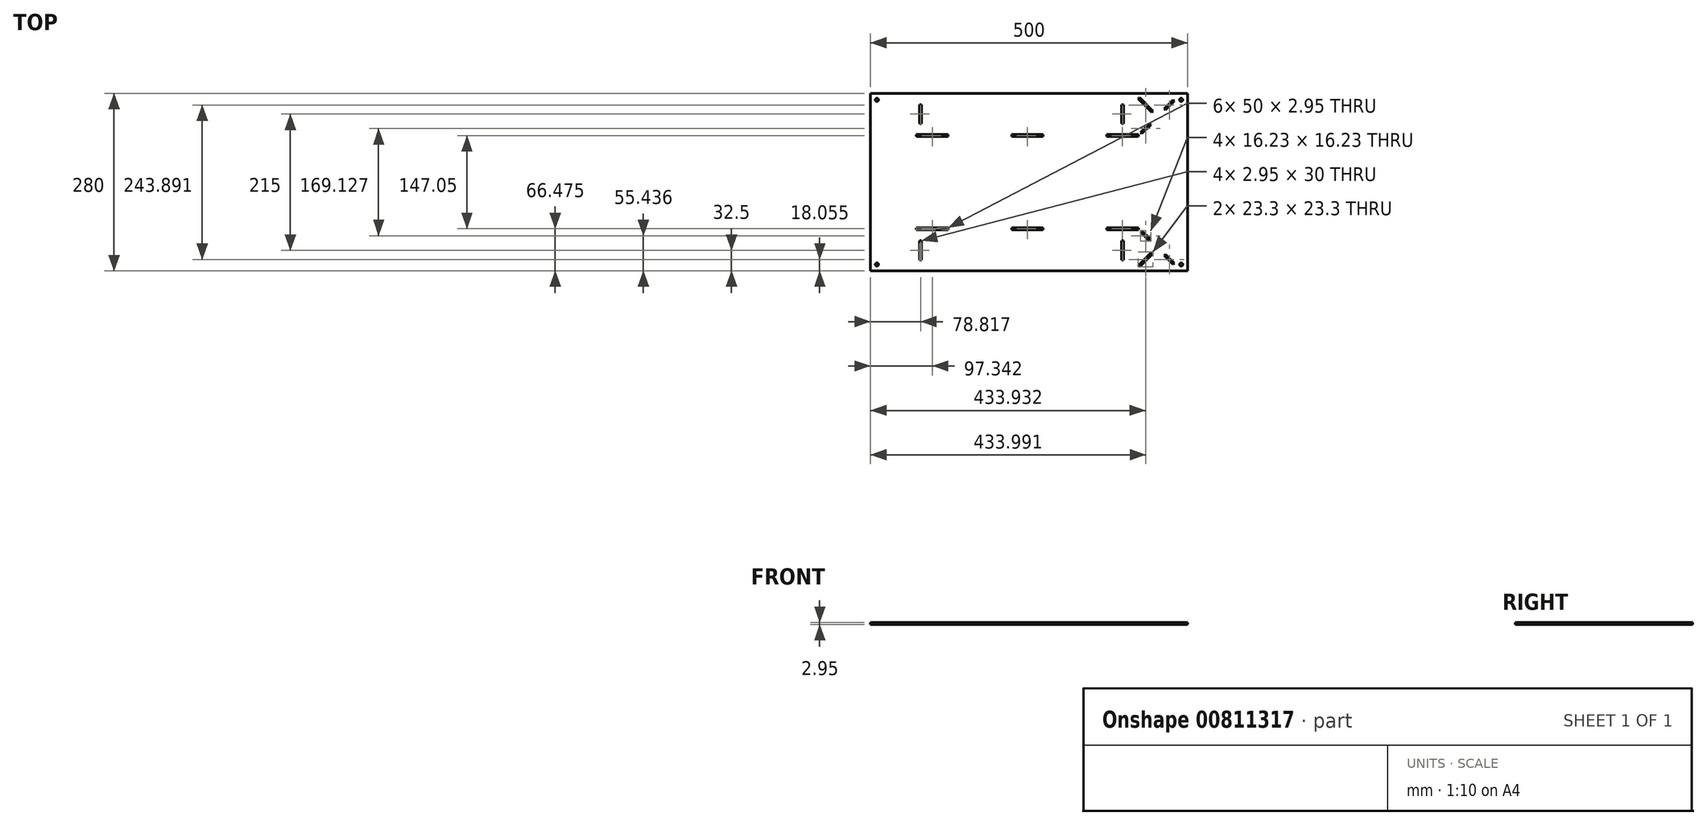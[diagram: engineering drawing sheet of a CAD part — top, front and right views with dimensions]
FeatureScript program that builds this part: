
annotation { "Feature Type Name" : "Feature", "Feature Type Description" : "" }
export const myFeature = defineFeature(function(context is Context, id is Id, definition is map)
    precondition{}
    {
        {
            var Q0;
            Q0=qCreatedBy(makeId("Top.planeOp"),FACE);
            var sketch = newSketch(context, id + "F0", { "sketchPlane" : qUnion([Q0])});
            skLineSegment(sketch, "E0.bottom", {"start": v(12.1, 0) * mm, "end": v(462.1, 0) * mm});
            skLineSegment(sketch, "E0.top", {"start": v(62.1, 280) * mm, "end": v(462.1, 280) * mm});
            skLineSegment(sketch, "E0.right", {"start": v(462.1, 0) * mm, "end": v(462.1, 280) * mm});
            skLineSegment(sketch, "E1.bottom", {"start": v(184.43, 215) * mm, "end": v(234.43, 215) * mm});
            skLineSegment(sketch, "E1.top", {"start": v(184.43, 212.05) * mm, "end": v(234.43, 212.05) * mm});
            skLineSegment(sketch, "E1.left", {"start": v(184.43, 215) * mm, "end": v(184.43, 212.05) * mm});
            skLineSegment(sketch, "E1.right", {"start": v(234.43, 215) * mm, "end": v(234.43, 212.05) * mm});
            skLineSegment(sketch, "E2.MirrorCS", {"start": v(334.43, 215) * mm, "end": v(334.43, 215) * mm});
            skLineSegment(sketch, "E3.MirrorCS", {"start": v(134.43, 65) * mm, "end": v(234.43, 65) * mm});
            skLineSegment(sketch, "E4.MirrorCS", {"start": v(334.43, 65) * mm, "end": v(334.43, 65) * mm});
            skLineSegment(sketch, "E5.bottom", {"start": v(358.36, 262.5) * mm, "end": v(361.3, 262.5) * mm});
            skLineSegment(sketch, "E5.top", {"start": v(358.36, 232.5) * mm, "end": v(361.3, 232.5) * mm});
            skLineSegment(sketch, "E5.left", {"start": v(358.36, 262.5) * mm, "end": v(358.36, 232.5) * mm});
            skLineSegment(sketch, "E5.right", {"start": v(361.3, 262.5) * mm, "end": v(361.3, 232.5) * mm});
            skLineSegment(sketch, "E6.bottom", {"start": v(334.43, 215) * mm, "end": v(384.43, 215) * mm});
            skLineSegment(sketch, "E6.top", {"start": v(334.43, 212.05) * mm, "end": v(384.43, 212.05) * mm});
            skLineSegment(sketch, "E6.left", {"start": v(334.43, 215) * mm, "end": v(334.43, 212.05) * mm});
            skLineSegment(sketch, "E6.right", {"start": v(384.43, 215) * mm, "end": v(384.43, 212.05) * mm});
            skLineSegment(sketch, "E7.bottom", {"start": v(234.43, 65) * mm, "end": v(184.43, 65) * mm});
            skLineSegment(sketch, "E7.top", {"start": v(234.43, 67.95) * mm, "end": v(184.43, 67.95) * mm});
            skLineSegment(sketch, "E7.left", {"start": v(234.43, 65) * mm, "end": v(234.43, 67.95) * mm});
            skLineSegment(sketch, "E7.right", {"start": v(184.43, 65) * mm, "end": v(184.43, 67.95) * mm});
            skLineSegment(sketch, "E8.bottom", {"start": v(334.43, 65) * mm, "end": v(384.43, 65) * mm});
            skLineSegment(sketch, "E8.top", {"start": v(334.43, 67.95) * mm, "end": v(384.43, 67.95) * mm});
            skLineSegment(sketch, "E8.left", {"start": v(334.43, 65) * mm, "end": v(334.43, 67.95) * mm});
            skLineSegment(sketch, "E8.right", {"start": v(384.43, 65) * mm, "end": v(384.43, 67.95) * mm});
            skLineSegment(sketch, "E9.bottom", {"start": v(358.36, 47.5) * mm, "end": v(361.3, 47.5) * mm});
            skLineSegment(sketch, "E9.top", {"start": v(358.36, 17.5) * mm, "end": v(361.3, 17.5) * mm});
            skLineSegment(sketch, "E9.left", {"start": v(358.36, 47.5) * mm, "end": v(358.36, 17.5) * mm});
            skLineSegment(sketch, "E9.right", {"start": v(361.3, 47.5) * mm, "end": v(361.3, 17.5) * mm});
            skLineSegment(sketch, "E10.bottom", {"start": v(62.1, 280) * mm, "end": v(-37.9, 280) * mm});
            skLineSegment(sketch, "E10.top", {"start": v(12.1, 0) * mm, "end": v(-37.9, 0) * mm});
            skLineSegment(sketch, "E10.right", {"start": v(-37.9, 280) * mm, "end": v(-37.9, 0) * mm});
            skLineSegment(sketch, "E11.bottom", {"start": v(84.43, 215) * mm, "end": v(34.43, 215) * mm});
            skLineSegment(sketch, "E11.top", {"start": v(84.43, 212.05) * mm, "end": v(34.43, 212.05) * mm});
            skLineSegment(sketch, "E11.left", {"start": v(84.43, 215) * mm, "end": v(84.43, 212.05) * mm});
            skLineSegment(sketch, "E11.right", {"start": v(34.43, 215) * mm, "end": v(34.43, 212.05) * mm});
            skLineSegment(sketch, "E12.bottom", {"start": v(84.43, 67.95) * mm, "end": v(34.43, 67.95) * mm});
            skLineSegment(sketch, "E12.top", {"start": v(84.43, 65) * mm, "end": v(34.43, 65) * mm});
            skLineSegment(sketch, "E12.left", {"start": v(84.43, 67.95) * mm, "end": v(84.43, 65) * mm});
            skLineSegment(sketch, "E12.right", {"start": v(34.43, 67.95) * mm, "end": v(34.43, 65) * mm});
            skLineSegment(sketch, "E13.bottom", {"start": v(39.43, 262.5) * mm, "end": v(42.38, 262.5) * mm});
            skLineSegment(sketch, "E13.top", {"start": v(39.43, 232.5) * mm, "end": v(42.38, 232.5) * mm});
            skLineSegment(sketch, "E13.left", {"start": v(39.43, 262.5) * mm, "end": v(39.43, 232.5) * mm});
            skLineSegment(sketch, "E13.right", {"start": v(42.38, 262.5) * mm, "end": v(42.38, 232.5) * mm});
            skLineSegment(sketch, "E14.bottom", {"start": v(39.43, 47.5) * mm, "end": v(42.38, 47.5) * mm});
            skLineSegment(sketch, "E14.top", {"start": v(39.43, 17.5) * mm, "end": v(42.38, 17.5) * mm});
            skLineSegment(sketch, "E14.left", {"start": v(39.43, 47.5) * mm, "end": v(39.43, 17.5) * mm});
            skLineSegment(sketch, "E14.right", {"start": v(42.38, 47.5) * mm, "end": v(42.38, 17.5) * mm});
            skSolve(sketch);
        }
        {
            var Q0;
            Q0=makeQuery(id+"F0.imprint","IMPRINT",FACE,{"disambiguationData":[TD([[makeQuery(id+"F0.imprint","IMPRINT",EDGE,{"derivedFrom":sQuery(id+"F0.wireOp",EDGE,"E0.bottom")}),1.0]])]});
            extrude(context, id + "F1", {"entities" : qUnion([Q0]), "depth" : 2.95 * mm, "offsetDistance" : 25 * mm});
        }
        {
            var Q0;
            Q0=makeQuery(id+"F1.opExtrude","CAP_FACE",FACE,{"disambiguationData":[OSD([sQuery(id+"F0.wireOp",EDGE,"E0.bottom"),sQuery(id+"F0.wireOp",EDGE,"E0.top"),sQuery(id+"F0.wireOp",EDGE,"E0.left"),sQuery(id+"F0.wireOp",EDGE,"E0.right"),sQuery(id+"F0.wireOp",EDGE,"E1.bottom"),sQuery(id+"F0.wireOp",EDGE,"E1.top"),sQuery(id+"F0.wireOp",EDGE,"E1.left"),sQuery(id+"F0.wireOp",EDGE,"E1.right"),sQuery(id+"F0.wireOp",EDGE,"e73540e0-437e-4d11-b89e-325f1f7d4c790.MirrorCS"),sQuery(id+"F0.wireOp",EDGE,"E2.MirrorCS"),sQuery(id+"F0.wireOp",EDGE,"06532218-7f8b-4a41-8e3c-2a9fed56a3b10.MirrorCS"),sQuery(id+"F0.wireOp",EDGE,"7cb798fc-15e8-495b-8a35-73028b4edfa90.MirrorCS"),sQuery(id+"F0.wireOp",EDGE,"545d7cc9-1fc7-4841-af53-376eaec099370.MirrorCS"),sQuery(id+"F0.wireOp",EDGE,"E3.MirrorCS"),sQuery(id+"F0.wireOp",EDGE,"9b8ca559-61c4-4ae6-86d6-e5e959e65d2c0.MirrorCS"),sQuery(id+"F0.wireOp",EDGE,"461afd8d-256b-4b3b-8858-7b4be28ac2ee0.MirrorCS"),sQuery(id+"F0.wireOp",EDGE,"ccdc6204-bf97-4cc3-8a27-938706aa7f700.MirrorCS"),sQuery(id+"F0.wireOp",EDGE,"E4.MirrorCS"),sQuery(id+"F0.wireOp",EDGE,"de380e3f-fddb-4eb0-9c14-f8c98a16e2c70.MirrorCS"),sQuery(id+"F0.wireOp",EDGE,"ee423979-f3e1-44e8-98c6-b9dc3032ede40.MirrorCS"),sQuery(id+"F0.wireOp",EDGE,"E5.bottom"),sQuery(id+"F0.wireOp",EDGE,"E5.top"),sQuery(id+"F0.wireOp",EDGE,"E5.left"),sQuery(id+"F0.wireOp",EDGE,"E5.right"),sQuery(id+"F0.wireOp",EDGE,"2a4d6bfd-6cea-46ef-a5a2-565ee4e24cbc0.MirrorCS"),sQuery(id+"F0.wireOp",EDGE,"e7e3dcee-2f9a-4279-8a5c-00eaed48cf630.MirrorCS"),sQuery(id+"F0.wireOp",EDGE,"b1a6a120-30f8-47bb-a578-e070e3f1ff540.MirrorCS"),sQuery(id+"F0.wireOp",EDGE,"80d5920c-4993-49ba-a786-e7242780b6720.MirrorCS")])],"isStart":false});
            var sketch = newSketch(context, id + "F2", { "sketchPlane" : qUnion([Q0])});
            skPoint(sketch, "E15", {"position": v(-27.9, 10) * mm});
            skPoint(sketch, "E16", {"position": v(-27.9, 270) * mm});
            skPoint(sketch, "E17", {"position": v(452.1, 270) * mm});
            skPoint(sketch, "E18", {"position": v(452.1, 10) * mm});
            skSolve(sketch);
        }
        {
            var Q0;
            Q0=sQuery(id+"F2.wireOp",VERTEX,"E15");
            var Q1;
            Q1=sQuery(id+"F2.wireOp",VERTEX,"E16");
            var Q2;
            Q2=sQuery(id+"F2.wireOp",VERTEX,"E18");
            var Q3;
            Q3=sQuery(id+"F2.wireOp",VERTEX,"E17");
            var Q4;
            Q4=makeQuery(id+"F1.opExtrude","SWEPT_BODY",BODY,{"disambiguationData":[OSD([sQuery(id+"F0.wireOp",EDGE,"E0.bottom"),sQuery(id+"F0.wireOp",EDGE,"E0.top"),sQuery(id+"F0.wireOp",EDGE,"E0.left"),sQuery(id+"F0.wireOp",EDGE,"E0.right"),sQuery(id+"F0.wireOp",EDGE,"E1.bottom"),sQuery(id+"F0.wireOp",EDGE,"E1.top"),sQuery(id+"F0.wireOp",EDGE,"E1.left"),sQuery(id+"F0.wireOp",EDGE,"E1.right"),sQuery(id+"F0.wireOp",EDGE,"e73540e0-437e-4d11-b89e-325f1f7d4c790.MirrorCS"),sQuery(id+"F0.wireOp",EDGE,"E2.MirrorCS"),sQuery(id+"F0.wireOp",EDGE,"06532218-7f8b-4a41-8e3c-2a9fed56a3b10.MirrorCS"),sQuery(id+"F0.wireOp",EDGE,"7cb798fc-15e8-495b-8a35-73028b4edfa90.MirrorCS"),sQuery(id+"F0.wireOp",EDGE,"545d7cc9-1fc7-4841-af53-376eaec099370.MirrorCS"),sQuery(id+"F0.wireOp",EDGE,"E3.MirrorCS"),sQuery(id+"F0.wireOp",EDGE,"9b8ca559-61c4-4ae6-86d6-e5e959e65d2c0.MirrorCS"),sQuery(id+"F0.wireOp",EDGE,"461afd8d-256b-4b3b-8858-7b4be28ac2ee0.MirrorCS"),sQuery(id+"F0.wireOp",EDGE,"ccdc6204-bf97-4cc3-8a27-938706aa7f700.MirrorCS"),sQuery(id+"F0.wireOp",EDGE,"E4.MirrorCS"),sQuery(id+"F0.wireOp",EDGE,"de380e3f-fddb-4eb0-9c14-f8c98a16e2c70.MirrorCS"),sQuery(id+"F0.wireOp",EDGE,"ee423979-f3e1-44e8-98c6-b9dc3032ede40.MirrorCS"),sQuery(id+"F0.wireOp",EDGE,"E5.bottom"),sQuery(id+"F0.wireOp",EDGE,"E5.top"),sQuery(id+"F0.wireOp",EDGE,"E5.left"),sQuery(id+"F0.wireOp",EDGE,"E5.right"),sQuery(id+"F0.wireOp",EDGE,"2a4d6bfd-6cea-46ef-a5a2-565ee4e24cbc0.MirrorCS"),sQuery(id+"F0.wireOp",EDGE,"e7e3dcee-2f9a-4279-8a5c-00eaed48cf630.MirrorCS"),sQuery(id+"F0.wireOp",EDGE,"b1a6a120-30f8-47bb-a578-e070e3f1ff540.MirrorCS"),sQuery(id+"F0.wireOp",EDGE,"80d5920c-4993-49ba-a786-e7242780b6720.MirrorCS")])]});
            hole(context, id + "F3", {"style" : HoleStyle.SIMPLE, "endStyle" : HoleEndStyle.THROUGH, "holeDiameter" : 5 * mm, "majorDiameter" : 5 * mm, "isTappedThrough" : true, "tappedDepth" : 12 * mm, "tapClearance" : 3, "locations" : qUnion([Q0, Q1, Q2, Q3]), "scope" : qUnion([Q4])});
        }
        {
            var Q0;
            Q0=makeQuery(id+"F1.opExtrude","CAP_FACE",FACE,{"disambiguationData":[OSD([sQuery(id+"F0.wireOp",EDGE,"E0.bottom"),sQuery(id+"F0.wireOp",EDGE,"E0.top"),sQuery(id+"F0.wireOp",EDGE,"E0.left"),sQuery(id+"F0.wireOp",EDGE,"E0.right"),sQuery(id+"F0.wireOp",EDGE,"E1.bottom"),sQuery(id+"F0.wireOp",EDGE,"E1.top"),sQuery(id+"F0.wireOp",EDGE,"E1.left"),sQuery(id+"F0.wireOp",EDGE,"E1.right"),sQuery(id+"F0.wireOp",EDGE,"E5.bottom"),sQuery(id+"F0.wireOp",EDGE,"E5.top"),sQuery(id+"F0.wireOp",EDGE,"E5.left"),sQuery(id+"F0.wireOp",EDGE,"E5.right"),sQuery(id+"F0.wireOp",EDGE,"E6.bottom"),sQuery(id+"F0.wireOp",EDGE,"E6.top"),sQuery(id+"F0.wireOp",EDGE,"E6.left"),sQuery(id+"F0.wireOp",EDGE,"E6.right"),sQuery(id+"F0.wireOp",EDGE,"E7.bottom"),sQuery(id+"F0.wireOp",EDGE,"E7.top"),sQuery(id+"F0.wireOp",EDGE,"E7.left"),sQuery(id+"F0.wireOp",EDGE,"E7.right"),sQuery(id+"F0.wireOp",EDGE,"E8.bottom"),sQuery(id+"F0.wireOp",EDGE,"E8.top"),sQuery(id+"F0.wireOp",EDGE,"E8.left"),sQuery(id+"F0.wireOp",EDGE,"E8.right"),sQuery(id+"F0.wireOp",EDGE,"E9.bottom"),sQuery(id+"F0.wireOp",EDGE,"E9.top"),sQuery(id+"F0.wireOp",EDGE,"E9.left"),sQuery(id+"F0.wireOp",EDGE,"E9.right")])],"isStart":false});
            var sketch = newSketch(context, id + "F4", { "sketchPlane" : qUnion([Q0])});
            skLineSegment(sketch, "E19", {"start": v(384.43, 215) * mm, "end": v(402.1, 232.68) * mm});
            skLineSegment(sketch, "E20", {"start": v(439.43, 270) * mm, "end": v(441.52, 267.91) * mm});
            skLineSegment(sketch, "E21", {"start": v(441.52, 267.91) * mm, "end": v(427.38, 253.77) * mm});
            skLineSegment(sketch, "E22", {"start": v(390.05, 216.45) * mm, "end": v(387.97, 218.54) * mm});
            skLineSegment(sketch, "E23", {"start": v(402.1, 232.68) * mm, "end": v(404.2, 230.6) * mm});
            skLineSegment(sketch, "E24", {"start": v(425.29, 255.86) * mm, "end": v(427.38, 253.77) * mm});
            skLineSegment(sketch, "E25.trimOffspring", {"start": v(425.29, 255.86) * mm, "end": v(439.43, 270) * mm});
            skLineSegment(sketch, "E26.trimOffspring", {"start": v(404.2, 230.6) * mm, "end": v(390.05, 216.45) * mm});
            skPoint(sketch, "E27", {"position": v(413.7, 244.27) * mm});
            skLineSegment(sketch, "E28", {"start": v(383.8, 270.94) * mm, "end": v(384.37, 271.5) * mm});
            skLineSegment(sketch, "E29", {"start": v(384.37, 271.5) * mm, "end": v(405.59, 250.3) * mm});
            skLineSegment(sketch, "E30", {"start": v(407.67, 252.38) * mm, "end": v(405.59, 250.3) * mm});
            skLineSegment(sketch, "E31", {"start": v(407.67, 252.38) * mm, "end": v(386.46, 273.6) * mm});
            skLineSegment(sketch, "E32", {"start": v(383.8, 270.94) * mm, "end": v(386.46, 273.6) * mm});
            skLineSegment(sketch, "E33", {"start": v(462.1, 140) * mm, "end": v(-37.9, 140) * mm});
            skLineSegment(sketch, "E34.MirrorCS", {"start": v(407.67, 27.62) * mm, "end": v(405.59, 29.7) * mm});
            skLineSegment(sketch, "E35.MirrorCS", {"start": v(425.29, 24.14) * mm, "end": v(427.38, 26.23) * mm});
            skLineSegment(sketch, "E36.MirrorCS", {"start": v(402.1, 47.32) * mm, "end": v(404.2, 49.4) * mm});
            skLineSegment(sketch, "E37.MirrorCS", {"start": v(439.43, 10) * mm, "end": v(441.52, 12.09) * mm});
            skLineSegment(sketch, "E38.MirrorCS", {"start": v(390.05, 63.55) * mm, "end": v(387.97, 61.46) * mm});
            skPoint(sketch, "E39.MirrorP", {"position": v(413.7, 35.73) * mm});
            skLineSegment(sketch, "E40.MirrorCS", {"start": v(407.67, 27.62) * mm, "end": v(386.46, 6.4) * mm});
            skLineSegment(sketch, "E41.MirrorCS", {"start": v(384.37, 8.5) * mm, "end": v(405.59, 29.7) * mm});
            skLineSegment(sketch, "E42.MirrorCS", {"start": v(404.2, 49.4) * mm, "end": v(390.05, 63.55) * mm});
            skLineSegment(sketch, "E43.MirrorCS", {"start": v(425.29, 24.14) * mm, "end": v(439.43, 10) * mm});
            skLineSegment(sketch, "E44.MirrorCS", {"start": v(384.43, 65) * mm, "end": v(402.1, 47.32) * mm});
            skLineSegment(sketch, "E45.MirrorCS", {"start": v(441.52, 12.09) * mm, "end": v(427.38, 26.23) * mm});
            skLineSegment(sketch, "E46", {"start": v(384.37, 8.5) * mm, "end": v(386.46, 6.4) * mm});
            skSolve(sketch);
        }
        {
            var Q0;
            Q0=makeQuery(id+"F4.imprint","IMPRINT",FACE,{"disambiguationData":[TD([[makeQuery(id+"F4.imprint","IMPRINT",EDGE,{"derivedFrom":sQuery(id+"F4.wireOp",EDGE,"E28")}),-1.0]])]});
            var Q1;
            Q1=makeQuery(id+"F4.imprint","IMPRINT",FACE,{"disambiguationData":[TD([[makeQuery(id+"F4.imprint","IMPRINT",EDGE,{"derivedFrom":sQuery(id+"F4.wireOp",EDGE,"E20")}),-1.0]])]});
            var Q2;
            {var subQ2=sQuery(id+"F4.wireOp",EDGE,"E22");Q2=makeQuery(id+"F4.imprint","IMPRINT",FACE,{"disambiguationData":[TD([[makeQuery(id+"F4.imprint","IMPRINT",EDGE,{"derivedFrom":subQ2}),-1.0]])]});}
            var Q3;
            {var subQ0=sQuery(id+"F4.wireOp",EDGE,"a934c7fb-54da-4184-a665-6b071d04c7bb2.MirrorCS");Q3=makeQuery(id+"F4.imprint","IMPRINT",FACE,{"disambiguationData":[TD([[makeQuery(id+"F4.imprint","IMPRINT",EDGE,{"derivedFrom":subQ0}),1.0]])]});}
            var Q4;
            Q4=makeQuery(id+"F4.imprint","IMPRINT",FACE,{"disambiguationData":[TD([[makeQuery(id+"F4.imprint","IMPRINT",EDGE,{"derivedFrom":sQuery(id+"F4.wireOp",EDGE,"a934c7fb-54da-4184-a665-6b071d04c7bb0.MirrorCS")}),1.0]])]});
            var Q5;
            Q5=makeQuery(id+"F4.imprint","IMPRINT",FACE,{"disambiguationData":[TD([[makeQuery(id+"F4.imprint","IMPRINT",EDGE,{"derivedFrom":sQuery(id+"F4.wireOp",EDGE,"a934c7fb-54da-4184-a665-6b071d04c7bb1.MirrorCS")}),1.0]])]});
            var Q6;
            Q6=makeQuery(id+"F4.imprint","IMPRINT",FACE,{"disambiguationData":[TD([[makeQuery(id+"F4.imprint","IMPRINT",EDGE,{"derivedFrom":sQuery(id+"F4.wireOp",EDGE,"E29")}),1.0]])]});
            var Q7;
            {var subQ0=sQuery(id+"F4.wireOp",EDGE,"E36.MirrorCS");Q7=makeQuery(id+"F4.imprint","IMPRINT",FACE,{"disambiguationData":[TD([[makeQuery(id+"F4.imprint","IMPRINT",EDGE,{"derivedFrom":subQ0}),1.0]])]});}
            var Q8;
            Q8=makeQuery(id+"F4.imprint","IMPRINT",FACE,{"disambiguationData":[TD([[makeQuery(id+"F4.imprint","IMPRINT",EDGE,{"derivedFrom":sQuery(id+"F4.wireOp",EDGE,"1635eeff-78d1-47ad-890c-4341ff0cacbf0.MirrorCS")}),1.0]])]});
            var Q9;
            Q9=makeQuery(id+"F4.imprint","IMPRINT",FACE,{"disambiguationData":[TD([[makeQuery(id+"F4.imprint","IMPRINT",EDGE,{"derivedFrom":sQuery(id+"F4.wireOp",EDGE,"E35.MirrorCS")}),-1.0]])]});
            var Q10;
            Q10=makeQuery(id+"F4.imprint","IMPRINT",FACE,{"disambiguationData":[TD([[makeQuery(id+"F4.imprint","IMPRINT",EDGE,{"derivedFrom":sQuery(id+"F4.wireOp",EDGE,"E34.MirrorCS")}),1.0]])]});
            extrude(context, id + "F5", {"entities" : qUnion([Q0, Q1, Q2, Q3, Q4, Q5, Q6, Q7, Q8, Q9, Q10]), "operationType" : NewBodyOperationType.REMOVE, "oppositeDirection" : true, "depth" : 2.95 * mm, "offsetDistance" : 25 * mm});
        }
    });
